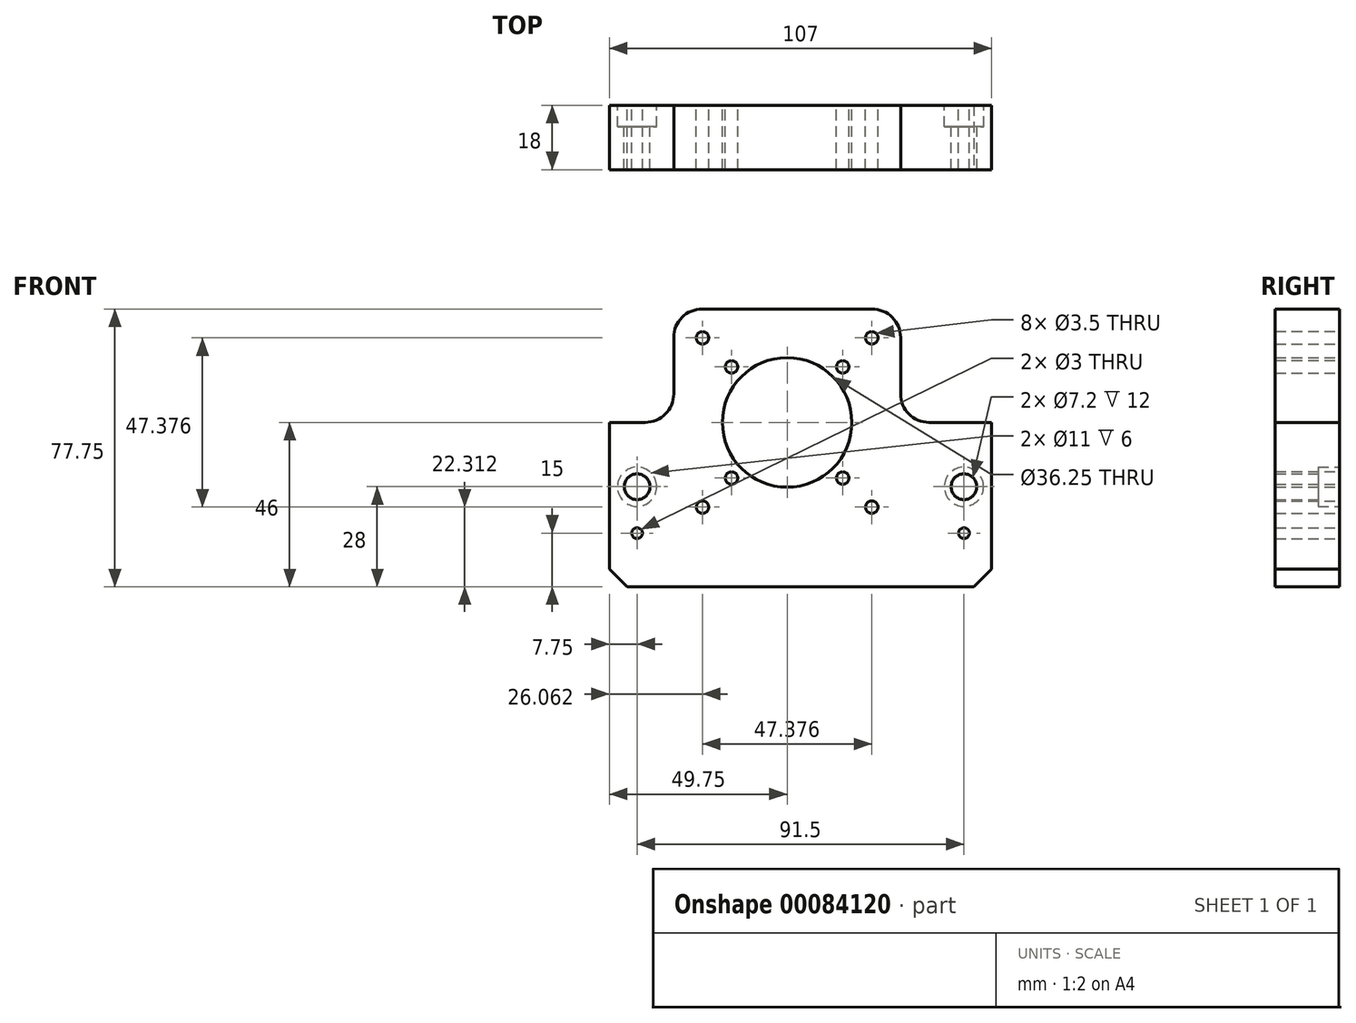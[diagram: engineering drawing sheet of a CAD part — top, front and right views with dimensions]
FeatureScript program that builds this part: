
annotation { "Feature Type Name" : "Feature", "Feature Type Description" : "" }
export const myFeature = defineFeature(function(context is Context, id is Id, definition is map)
    precondition{}
    {
        {
            var Q0;
            Q0=qCreatedBy(makeId("Front.planeOp"),FACE);
            var sketch = newSketch(context, id + "F0", { "sketchPlane" : qUnion([Q0])});
            skPoint(sketch, "E0.middle", {"position": v(0, 0) * mm});
            skCircle(sketch, "E1", {"center": v(0, 0) * mm, "radius": 18.12 * mm});
            skLineSegment(sketch, "E2", {"start": v(0, 0) * mm, "end": v(-42, 0) * mm, "construction": true});
            skPoint(sketch, "E3", {"position": v(-42, -18) * mm});
            skPoint(sketch, "E4", {"position": v(-42, -31) * mm});
            skCircle(sketch, "E5", {"center": v(-42, -31) * mm, "radius": 1.5 * mm});
            skLineSegment(sketch, "E6", {"start": v(0, 0) * mm, "end": v(49.5, 0) * mm, "construction": true});
            skPoint(sketch, "E7", {"position": v(49.5, -18) * mm});
            skPoint(sketch, "E8", {"position": v(49.5, -31) * mm});
            skCircle(sketch, "E9", {"center": v(49.5, -31) * mm, "radius": 1.5 * mm});
            skLineSegment(sketch, "E10.bottom", {"start": v(31.75, -31.75) * mm, "end": v(-31.75, -31.75) * mm});
            skLineSegment(sketch, "E10.top", {"start": v(31.75, 31.75) * mm, "end": v(-31.75, 31.75) * mm});
            skLineSegment(sketch, "E10.left", {"start": v(31.75, -31.75) * mm, "end": v(31.75, 31.75) * mm});
            skLineSegment(sketch, "E10.right", {"start": v(-31.75, -31.75) * mm, "end": v(-31.75, 31.75) * mm});
            skLineSegment(sketch, "E11", {"start": v(-31.75, 31.75) * mm, "end": v(0, 0) * mm, "construction": true});
            skCircle(sketch, "E12", {"center": v(0, 0) * mm, "radius": 22 * mm, "construction": true});
            skCircle(sketch, "E13", {"center": v(0, 0) * mm, "radius": 33.5 * mm, "construction": true});
            skCircle(sketch, "E14", {"center": v(-15.56, 15.56) * mm, "radius": 1.75 * mm});
            skCircle(sketch, "E15", {"center": v(-23.69, 23.69) * mm, "radius": 1.75 * mm});
            skCircle(sketch, "E16.1.0", {"center": v(-15.56, -15.56) * mm, "radius": 1.75 * mm});
            skCircle(sketch, "E16.2.0", {"center": v(15.56, -15.56) * mm, "radius": 1.75 * mm});
            skCircle(sketch, "E16.3.0", {"center": v(15.56, 15.56) * mm, "radius": 1.75 * mm});
            skCircle(sketch, "E17.1.0", {"center": v(-23.69, -23.69) * mm, "radius": 1.75 * mm});
            skCircle(sketch, "E17.2.0", {"center": v(23.69, -23.69) * mm, "radius": 1.75 * mm});
            skCircle(sketch, "E17.3.0", {"center": v(23.69, 23.69) * mm, "radius": 1.75 * mm});
            skLineSegment(sketch, "E18", {"start": v(-42, -18) * mm, "end": v(49.5, -18) * mm, "construction": true});
            skPoint(sketch, "E19", {"position": v(3.75, -18) * mm});
            skLineSegment(sketch, "E20.bottom", {"start": v(57.25, -46) * mm, "end": v(-49.75, -46) * mm});
            skLineSegment(sketch, "E21", {"start": v(57.25, -46) * mm, "end": v(57.25, 0) * mm});
            skLineSegment(sketch, "E22", {"start": v(57.25, 0) * mm, "end": v(-49.75, 0) * mm});
            skLineSegment(sketch, "E23", {"start": v(-49.75, 0) * mm, "end": v(-49.75, -46) * mm});
            skSolve(sketch);
        }
        {
            var Q0;
            {var subQ1=sQuery(id+"F0.wireOp",EDGE,"E0.bottom");Q0=makeQuery(id+"F0.imprint","IMPRINT",FACE,{"disambiguationData":[TD([[makeQuery(id+"F0.imprint","IMPRINT",EDGE,{"derivedFrom":subQ1}),-1.0]])]});}
            var Q1;
            Q1=makeQuery(id+"F0.imprint","IMPRINT",FACE,{"disambiguationData":[TD([[makeQuery(id+"F0.imprint","IMPRINT",EDGE,{"derivedFrom":sQuery(id+"F0.wireOp",EDGE,"ySye2NLZ-D5D7-gAEp-k93w-C5qcBxg8X62D")}),-1.0]])]});
            var Q2;
            {var subQ12=sQuery(id+"F0.wireOp",EDGE,"E10.top");Q2=makeQuery(id+"F0.imprint","IMPRINT",FACE,{"disambiguationData":[TD([[makeQuery(id+"F0.imprint","IMPRINT",EDGE,{"derivedFrom":subQ12}),1.0]])]});}
            var Q3;
            {var subQ8=sQuery(id+"F0.wireOp",EDGE,"E10.bottom");Q3=makeQuery(id+"F0.imprint","IMPRINT",FACE,{"disambiguationData":[TD([[makeQuery(id+"F0.imprint","IMPRINT",EDGE,{"derivedFrom":subQ8}),-1.0]])]});}
            var Q4;
            Q4=makeQuery(id+"F0.imprint","IMPRINT",FACE,{"disambiguationData":[TD([[makeQuery(id+"F0.imprint","IMPRINT",EDGE,{"derivedFrom":sQuery(id+"F0.wireOp",EDGE,"E5")}),-1.0]])]});
            extrude(context, id + "F1", {"entities" : qUnion([Q0, Q1, Q2, Q3, Q4]), "depth" : 18 * mm});
        }
        {
            var Q0;
            Q0=makeQuery(id+"F1.opExtrude","SWEPT_EDGE",EDGE,{"disambiguationData":[OSD([sQuery(id+"F0.wireOp",EDGE,"E20.bottom"),sQuery(id+"F0.wireOp",EDGE,"E20.right")])]});
            var Q1;
            Q1=makeQuery(id+"F1.opExtrude","SWEPT_EDGE",EDGE,{"disambiguationData":[OSD([sQuery(id+"F0.wireOp",EDGE,"E20.bottom"),sQuery(id+"F0.wireOp",EDGE,"E20.left")])]});
            chamfer(context, id + "F2", {"entities" : qUnion([Q0, Q1]), "width" : 5 * mm, "tangentPropagation" : true});
        }
        {
            var Q0;
            Q0=makeQuery(id+"F1.opExtrude","SWEPT_EDGE",EDGE,{"disambiguationData":[OSD([sQuery(id+"F0.wireOp",EDGE,"E10.left"),sQuery(id+"F0.wireOp",EDGE,"E20.top")])]});
            var Q1;
            Q1=makeQuery(id+"F1.opExtrude","SWEPT_EDGE",EDGE,{"disambiguationData":[OSD([sQuery(id+"F0.wireOp",EDGE,"E10.right"),sQuery(id+"F0.wireOp",EDGE,"E20.top")])]});
            fillet(context, id + "F3", {"entities" : qUnion([Q0, Q1]), "radius" : 8 * mm, "tangentPropagation" : true, "allowEdgeOverflow" : false});
        }
        {
            var Q0;
            Q0=sQuery(id+"F0.wireOp",VERTEX,"E7");
            var Q1;
            Q1=sQuery(id+"F0.wireOp",VERTEX,"E3");
            var Q2;
            Q2=makeQuery(id+"F1.opExtrude","SWEPT_BODY",BODY,{"disambiguationData":[OSD([sQuery(id+"F0.wireOp",EDGE,"E1"),sQuery(id+"F0.wireOp",EDGE,"E5"),sQuery(id+"F0.wireOp",EDGE,"E9"),sQuery(id+"F0.wireOp",EDGE,"E10.top"),sQuery(id+"F0.wireOp",EDGE,"E10.left"),sQuery(id+"F0.wireOp",EDGE,"E10.right"),sQuery(id+"F0.wireOp",EDGE,"E14"),sQuery(id+"F0.wireOp",EDGE,"E15"),sQuery(id+"F0.wireOp",EDGE,"E16.1.0"),sQuery(id+"F0.wireOp",EDGE,"E16.2.0"),sQuery(id+"F0.wireOp",EDGE,"E16.3.0"),sQuery(id+"F0.wireOp",EDGE,"E17.1.0"),sQuery(id+"F0.wireOp",EDGE,"E17.2.0"),sQuery(id+"F0.wireOp",EDGE,"E17.3.0"),sQuery(id+"F0.wireOp",EDGE,"E20.bottom"),sQuery(id+"F0.wireOp",EDGE,"E20.top"),sQuery(id+"F0.wireOp",EDGE,"E20.left"),sQuery(id+"F0.wireOp",EDGE,"E20.right")])]});
            hole(context, id + "F4", {"style" : HoleStyle.C_BORE, "endStyle" : HoleEndStyle.BLIND, "oppositeDirection" : true, "holeDiameter" : 7.2 * mm, "cBoreDiameter" : 11 * mm, "cBoreDepth" : 6 * mm, "holeDepth" : 35 * mm, "startFromSketch" : true, "locations" : qUnion([Q0, Q1]), "scope" : qUnion([Q2])});
        }
    });
